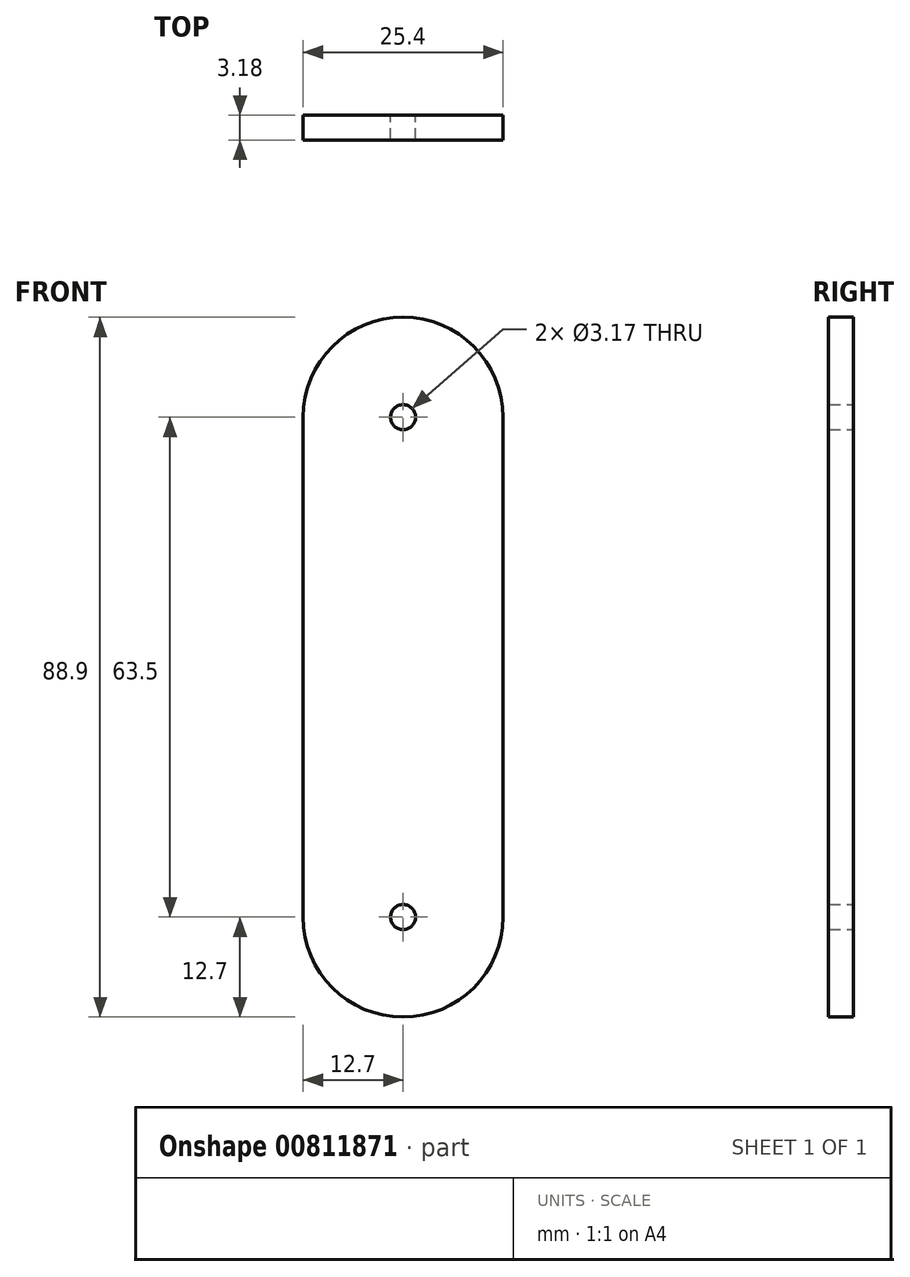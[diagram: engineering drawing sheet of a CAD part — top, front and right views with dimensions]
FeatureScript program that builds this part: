
annotation { "Feature Type Name" : "Feature", "Feature Type Description" : "" }
export const myFeature = defineFeature(function(context is Context, id is Id, definition is map)
    precondition{}
    {
        {
            var Q0;
            Q0=qCreatedBy(makeId("Front.planeOp"),FACE);
            var sketch = newSketch(context, id + "F0", { "sketchPlane" : qUnion([Q0])});
            skLineSegment(sketch, "E0.bottom", {"start": v(0, 44.45) * mm, "end": v(0, 44.45) * mm});
            skLineSegment(sketch, "E0.top", {"start": v(0, -44.45) * mm, "end": v(0, -44.45) * mm});
            skLineSegment(sketch, "E0.left", {"start": v(12.7, 31.75) * mm, "end": v(12.7, -31.75) * mm});
            skLineSegment(sketch, "E0.right", {"start": v(-12.7, 31.75) * mm, "end": v(-12.7, -31.75) * mm});
            skPoint(sketch, "E0.middle", {"position": v(0, 0) * mm});
            skPoint(sketch, "E1.visualSharp", {"position": v(-12.7, -44.45) * mm});
            skArc(sketch, "E1.filletArc", {"start": v(-12.7, -31.75) * mm, "mid": v(-8.98, -40.73) * mm, "end": v(0, -44.45) * mm});
            skPoint(sketch, "E2.visualSharp", {"position": v(12.7, -44.45) * mm});
            skArc(sketch, "E2.filletArc", {"start": v(0, -44.45) * mm, "mid": v(8.98, -40.73) * mm, "end": v(12.7, -31.75) * mm});
            skPoint(sketch, "E3.visualSharp", {"position": v(12.7, 44.45) * mm});
            skArc(sketch, "E3.filletArc", {"start": v(12.7, 31.75) * mm, "mid": v(8.98, 40.73) * mm, "end": v(0, 44.45) * mm});
            skPoint(sketch, "E4.visualSharp", {"position": v(-12.7, 44.45) * mm});
            skArc(sketch, "E4.filletArc", {"start": v(0, 44.45) * mm, "mid": v(-8.98, 40.73) * mm, "end": v(-12.7, 31.75) * mm});
            skCircle(sketch, "E5", {"center": v(0, 31.75) * mm, "radius": 1.59 * mm});
            skCircle(sketch, "E6", {"center": v(0, -31.75) * mm, "radius": 1.59 * mm});
            skSolve(sketch);
        }
        {
            var Q0;
            Q0=makeQuery(id+"F0.imprint","IMPRINT",FACE,{"disambiguationData":[TD([[makeQuery(id+"F0.imprint","IMPRINT",EDGE,{"derivedFrom":sQuery(id+"F0.wireOp",EDGE,"E0.left")}),-1.0]])]});
            extrude(context, id + "F1", {"entities" : qUnion([Q0]), "endBound" : BoundingType.SYMMETRIC, "depth" : 3.17 * mm, "offsetDistance" : 25.4 * mm});
        }
    });
